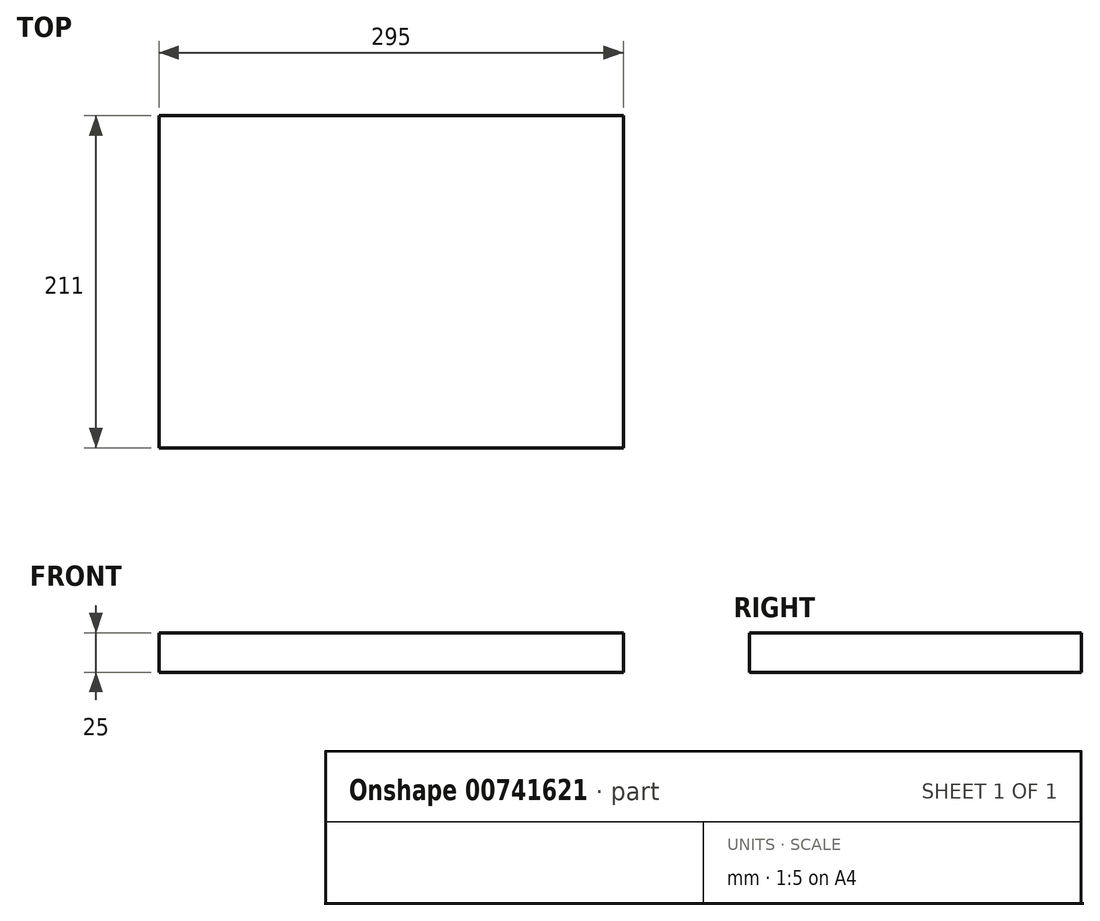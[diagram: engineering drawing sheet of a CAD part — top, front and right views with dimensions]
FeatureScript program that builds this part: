
annotation { "Feature Type Name" : "Feature", "Feature Type Description" : "" }
export const myFeature = defineFeature(function(context is Context, id is Id, definition is map)
    precondition{}
    {
        {
            var Q0;
            Q0=qCreatedBy(makeId("Top.planeOp"),FACE);
            var sketch = newSketch(context, id + "F0", { "sketchPlane" : qUnion([Q0])});
            skLineSegment(sketch, "E0.bottom", {"start": v(147.5, -105.5) * mm, "end": v(-147.5, -105.5) * mm});
            skLineSegment(sketch, "E0.top", {"start": v(147.5, 105.5) * mm, "end": v(-147.5, 105.5) * mm});
            skLineSegment(sketch, "E0.left", {"start": v(147.5, -105.5) * mm, "end": v(147.5, 105.5) * mm});
            skLineSegment(sketch, "E0.right", {"start": v(-147.5, -105.5) * mm, "end": v(-147.5, 105.5) * mm});
            skPoint(sketch, "E0.middle", {"position": v(0, 0) * mm});
            skSolve(sketch);
        }
        {
            var Q0;
            Q0=makeQuery(id+"F0.imprint","IMPRINT",FACE,{"disambiguationData":[TD([[makeQuery(id+"F0.imprint","IMPRINT",EDGE,{"derivedFrom":sQuery(id+"F0.wireOp",EDGE,"E0.bottom")}),-1.0]])]});
            extrude(context, id + "F1", {"entities" : qUnion([Q0]), "depth" : 25 * mm, "offsetDistance" : 25 * mm});
        }
    });
